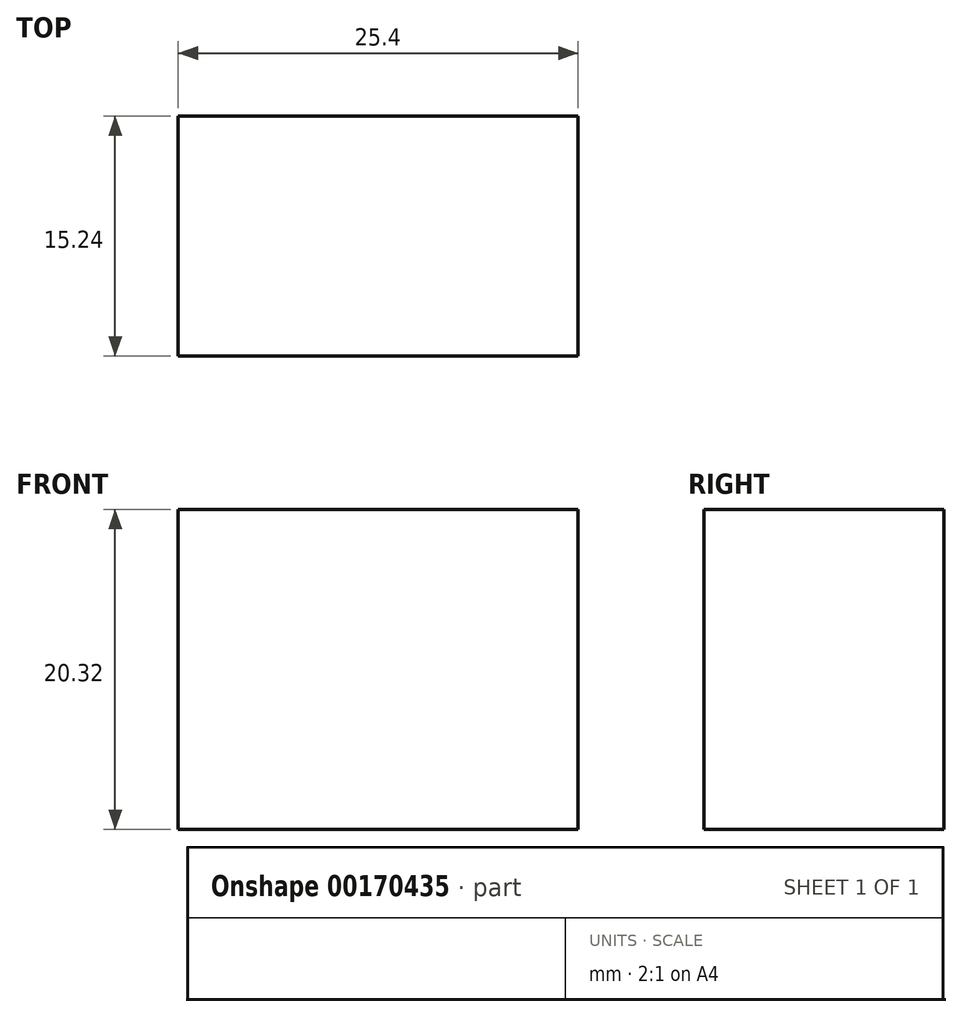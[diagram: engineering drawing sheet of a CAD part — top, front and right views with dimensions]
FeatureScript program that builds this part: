
annotation { "Feature Type Name" : "Feature", "Feature Type Description" : "" }
export const myFeature = defineFeature(function(context is Context, id is Id, definition is map)
    precondition{}
    {
        {
            var Q0;
            Q0=qCreatedBy(makeId("Top.planeOp"),FACE);
            var sketch = newSketch(context, id + "F0", { "sketchPlane" : qUnion([Q0])});
            skLineSegment(sketch, "E0.bottom", {"start": v(12.7, 7.62) * mm, "end": v(-12.7, 7.62) * mm});
            skLineSegment(sketch, "E0.top", {"start": v(12.7, -7.62) * mm, "end": v(-12.7, -7.62) * mm});
            skLineSegment(sketch, "E0.left", {"start": v(12.7, 7.62) * mm, "end": v(12.7, -7.62) * mm});
            skLineSegment(sketch, "E0.right", {"start": v(-12.7, 7.62) * mm, "end": v(-12.7, -7.62) * mm});
            skPoint(sketch, "E0.middle", {"position": v(0, 0) * mm});
            skSolve(sketch);
        }
        {
            var Q0;
            Q0 = qSketchRegion(id + "F0", true);
            extrude(context, id + "F1", {"entities" : qUnion([Q0]), "depth" : 20.32 * mm});
        }
    });
